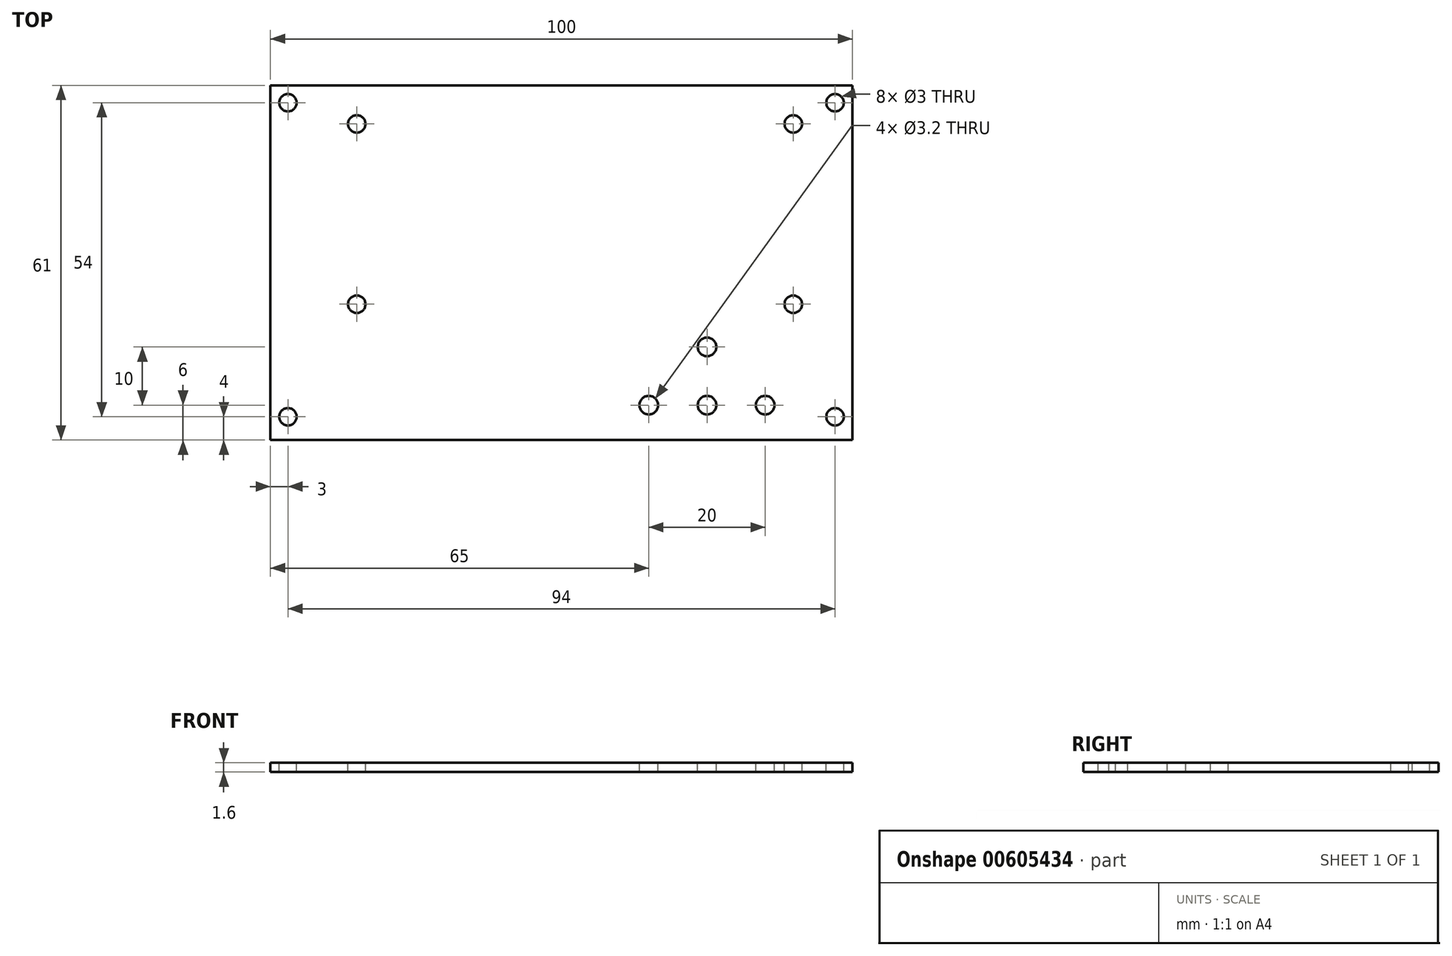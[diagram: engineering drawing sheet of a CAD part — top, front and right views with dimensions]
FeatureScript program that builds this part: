
annotation { "Feature Type Name" : "Feature", "Feature Type Description" : "" }
export const myFeature = defineFeature(function(context is Context, id is Id, definition is map)
    precondition{}
    {
        {
            var Q0;
            Q0=qCreatedBy(makeId("Top.planeOp"),FACE);
            var sketch = newSketch(context, id + "F0", { "sketchPlane" : qUnion([Q0])});
            skLineSegment(sketch, "E0.bottom", {"start": v(-50, -30) * mm, "end": v(50, -30) * mm});
            skLineSegment(sketch, "E0.top", {"start": v(-50, 30) * mm, "end": v(50, 30) * mm});
            skLineSegment(sketch, "E0.left", {"start": v(-50, -30) * mm, "end": v(-50, 30) * mm});
            skLineSegment(sketch, "E0.right", {"start": v(50, -30) * mm, "end": v(50, 30) * mm});
            skPoint(sketch, "E0.middle", {"position": v(0, 0) * mm});
            skCircle(sketch, "E1", {"center": v(-35.18, 23.35) * mm, "radius": 1.5 * mm});
            skCircle(sketch, "E2", {"center": v(39.83, 23.35) * mm, "radius": 1.5 * mm});
            skCircle(sketch, "E3", {"center": v(39.83, -7.65) * mm, "radius": 1.5 * mm});
            skCircle(sketch, "E4", {"center": v(-35.17, -7.65) * mm, "radius": 1.5 * mm});
            skCircle(sketch, "E5", {"center": v(15, -25) * mm, "radius": 1.6 * mm});
            skCircle(sketch, "E6", {"center": v(25, -25) * mm, "radius": 1.6 * mm});
            skCircle(sketch, "E7", {"center": v(35, -25) * mm, "radius": 1.6 * mm});
            skCircle(sketch, "E8", {"center": v(25, -15) * mm, "radius": 1.6 * mm});
            skCircle(sketch, "E9", {"center": v(-47, -27) * mm, "radius": 1.5 * mm});
            skCircle(sketch, "E10.MirrorC", {"center": v(47, -27) * mm, "radius": 1.5 * mm});
            skCircle(sketch, "E11.MirrorC", {"center": v(-47, 27) * mm, "radius": 1.5 * mm});
            skCircle(sketch, "E12.MirrorC", {"center": v(47, 27) * mm, "radius": 1.5 * mm});
            skLineSegment(sketch, "E13.top", {"start": v(-50, -31) * mm, "end": v(50, -31) * mm});
            skLineSegment(sketch, "E13.left", {"start": v(-50, -30) * mm, "end": v(-50, -31) * mm});
            skLineSegment(sketch, "E13.right", {"start": v(50, -30) * mm, "end": v(50, -31) * mm});
            skSolve(sketch);
        }
        {
            var Q0;
            Q0=makeQuery(id+"F0.imprint","IMPRINT",FACE,{"disambiguationData":[TD([[makeQuery(id+"F0.imprint","IMPRINT",EDGE,{"derivedFrom":sQuery(id+"F0.wireOp",EDGE,"E0.bottom")}),1.0]])]});
            var Q1;
            Q1=makeQuery(id+"F0.imprint","IMPRINT",FACE,{"disambiguationData":[TD([[makeQuery(id+"F0.imprint","IMPRINT",EDGE,{"derivedFrom":sQuery(id+"F0.wireOp",EDGE,"E0.bottom")}),-1.0]])]});
            var Q2;
            Q2=makeQuery(id+"F0.imprint","IMPRINT",FACE,{"disambiguationData":[TD([[makeQuery(id+"F0.imprint","IMPRINT",EDGE,{"derivedFrom":sQuery(id+"F0.wireOp",EDGE,"E0.top")}),-1.0]])]});
            extrude(context, id + "F1", {"entities" : qUnion([Q0, Q1, Q2]), "oppositeDirection" : true, "depth" : 1.6 * mm, "offsetDistance" : 25 * mm});
        }
    });
